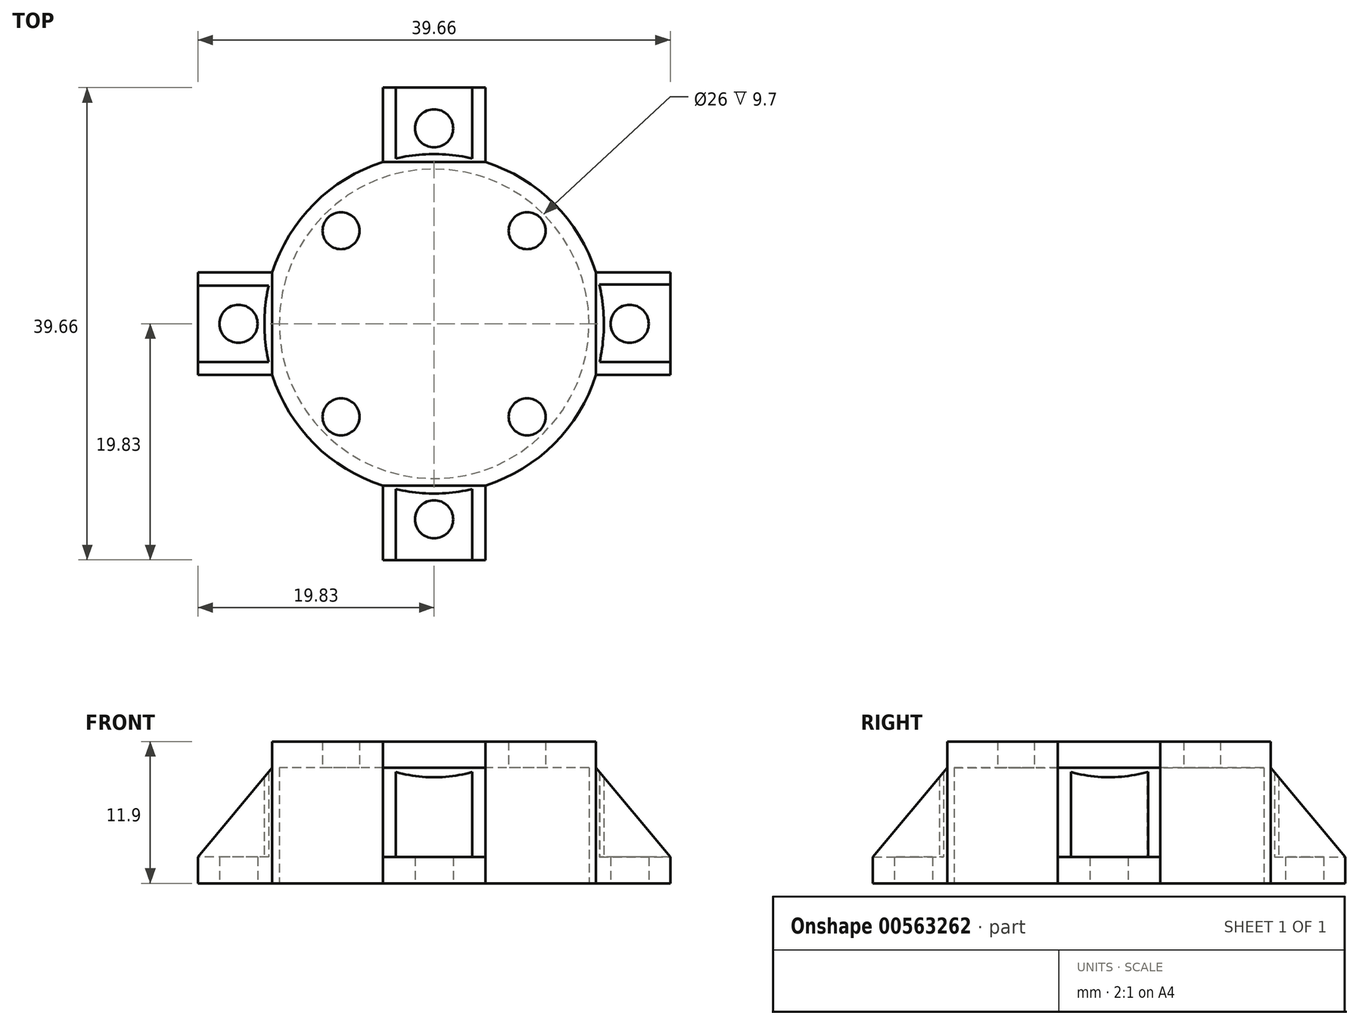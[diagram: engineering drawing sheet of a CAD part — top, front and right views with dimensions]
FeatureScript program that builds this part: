
annotation { "Feature Type Name" : "Feature", "Feature Type Description" : "" }
export const myFeature = defineFeature(function(context is Context, id is Id, definition is map)
    precondition{}
    {
        {
            var Q0;
            Q0=qCreatedBy(makeId("Top.planeOp"),FACE);
            var sketch = newSketch(context, id + "F0", { "sketchPlane" : qUnion([Q0])});
            skCircle(sketch, "E0", {"center": v(0, 0) * mm, "radius": 13 * mm});
            skLineSegment(sketch, "E1", {"start": v(0, 19.83) * mm, "end": v(4.3, 19.83) * mm});
            skLineSegment(sketch, "E2", {"start": v(4.3, 19.83) * mm, "end": v(4.3, 12.27) * mm});
            skLineSegment(sketch, "E3.MirrorCS", {"start": v(0, 19.83) * mm, "end": v(-4.3, 19.83) * mm});
            skLineSegment(sketch, "E4.MirrorCS", {"start": v(-4.3, 19.83) * mm, "end": v(-4.3, 12.27) * mm});
            skLineSegment(sketch, "E5", {"start": v(0, 0) * mm, "end": v(27.32, 0) * mm, "construction": true});
            skLineSegment(sketch, "E6", {"start": v(0, 0) * mm, "end": v(27.32, 27.32) * mm, "construction": true});
            skLineSegment(sketch, "E7", {"start": v(0, 19.83) * mm, "end": v(0, 13) * mm, "construction": true});
            skCircle(sketch, "E8", {"center": v(0, 16.42) * mm, "radius": 1.6 * mm});
            skLineSegment(sketch, "E9.MirrorCS", {"start": v(19.83, 0) * mm, "end": v(19.83, 4.3) * mm});
            skLineSegment(sketch, "E10.MirrorCS", {"start": v(19.83, 0) * mm, "end": v(19.83, -4.3) * mm});
            skLineSegment(sketch, "E11.MirrorCS", {"start": v(19.83, -4.3) * mm, "end": v(12.27, -4.3) * mm});
            skCircle(sketch, "E12.MirrorC", {"center": v(16.42, 0) * mm, "radius": 1.6 * mm});
            skLineSegment(sketch, "E13.MirrorCS", {"start": v(19.83, 4.3) * mm, "end": v(12.27, 4.3) * mm});
            skLineSegment(sketch, "E14.MirrorCS", {"start": v(0, -19.83) * mm, "end": v(4.3, -19.83) * mm});
            skLineSegment(sketch, "E15.MirrorCS", {"start": v(0, -19.83) * mm, "end": v(-4.3, -19.83) * mm});
            skLineSegment(sketch, "E16.MirrorCS", {"start": v(-4.3, -19.83) * mm, "end": v(-4.3, -12.27) * mm});
            skLineSegment(sketch, "E17.MirrorCS", {"start": v(4.3, -19.83) * mm, "end": v(4.3, -12.27) * mm});
            skCircle(sketch, "E18.MirrorC", {"center": v(0, -16.42) * mm, "radius": 1.6 * mm});
            skLineSegment(sketch, "E19", {"start": v(0, 0) * mm, "end": v(0, -28.1) * mm, "construction": true});
            skLineSegment(sketch, "E20.MirrorCS", {"start": v(-19.83, 4.3) * mm, "end": v(-12.27, 4.3) * mm});
            skLineSegment(sketch, "E21.MirrorCS", {"start": v(-19.83, 0) * mm, "end": v(-19.83, 4.3) * mm});
            skCircle(sketch, "E22.MirrorC", {"center": v(-16.42, 0) * mm, "radius": 1.6 * mm});
            skLineSegment(sketch, "E23.MirrorCS", {"start": v(-19.83, 0) * mm, "end": v(-19.83, -4.3) * mm});
            skLineSegment(sketch, "E24.MirrorCS", {"start": v(-19.83, -4.3) * mm, "end": v(-12.27, -4.3) * mm});
            skCircle(sketch, "E25", {"center": v(0, 0) * mm, "radius": 14.25 * mm});
            skSolve(sketch);
        }
        {
            var Q0;
            {var subQ5=sQuery(id+"F0.wireOp",EDGE,"E1");Q0=makeQuery(id+"F0.imprint","IMPRINT",FACE,{"disambiguationData":[TD([[makeQuery(id+"F0.imprint","IMPRINT",EDGE,{"derivedFrom":subQ5}),-1.0]])]});}
            var Q1;
            {var subQ0=sQuery(id+"F0.wireOp",EDGE,"E4.MirrorCS");var subQ1=sQuery(id+"F0.wireOp",EDGE,"E0");var subQ2=makeQuery(id+"F0.imprint","INTERSECT",VERTEX,{"derivedFrom":[subQ1,subQ0]});Q1=makeQuery(id+"F0.imprint","IMPRINT",FACE,{"disambiguationData":[TD([[makeQuery(id+"F0.imprint","IMPRINT",EDGE,{"disambiguationData":[TD([[subQ2,-1.0]])],"derivedFrom":subQ1}),-1.0]])]});}
            var Q2;
            {var subQ0=sQuery(id+"F0.wireOp",EDGE,"E2");var subQ1=sQuery(id+"F0.wireOp",EDGE,"E0");var subQ2=makeQuery(id+"F0.imprint","INTERSECT",VERTEX,{"derivedFrom":[subQ1,subQ0]});Q2=makeQuery(id+"F0.imprint","IMPRINT",FACE,{"disambiguationData":[TD([[makeQuery(id+"F0.imprint","IMPRINT",EDGE,{"disambiguationData":[TD([[subQ2,-1.0]])],"derivedFrom":subQ1}),-1.0]])]});}
            var Q3;
            {var subQ0=sQuery(id+"F0.wireOp",EDGE,"E2");var subQ1=sQuery(id+"F0.wireOp",EDGE,"E0");var subQ2=makeQuery(id+"F0.imprint","INTERSECT",VERTEX,{"derivedFrom":[subQ1,subQ0]});Q3=makeQuery(id+"F0.imprint","IMPRINT",FACE,{"disambiguationData":[TD([[makeQuery(id+"F0.imprint","IMPRINT",EDGE,{"disambiguationData":[TD([[subQ2,1.0]])],"derivedFrom":subQ1}),-1.0]])]});}
            var Q4;
            {var subQ0=sQuery(id+"F0.wireOp",EDGE,"E11.MirrorCS");var subQ1=sQuery(id+"F0.wireOp",EDGE,"E0");var subQ2=makeQuery(id+"F0.imprint","INTERSECT",VERTEX,{"derivedFrom":[subQ1,subQ0]});Q4=makeQuery(id+"F0.imprint","IMPRINT",FACE,{"disambiguationData":[TD([[makeQuery(id+"F0.imprint","IMPRINT",EDGE,{"disambiguationData":[TD([[subQ2,-1.0]])],"derivedFrom":subQ1}),-1.0]])]});}
            var Q5;
            {var subQ4=sQuery(id+"F0.wireOp",EDGE,"E9.MirrorCS");Q5=makeQuery(id+"F0.imprint","IMPRINT",FACE,{"disambiguationData":[TD([[makeQuery(id+"F0.imprint","IMPRINT",EDGE,{"derivedFrom":subQ4}),1.0]])]});}
            var Q6;
            {var subQ0=sQuery(id+"F0.wireOp",EDGE,"E11.MirrorCS");var subQ1=sQuery(id+"F0.wireOp",EDGE,"E0");var subQ2=makeQuery(id+"F0.imprint","INTERSECT",VERTEX,{"derivedFrom":[subQ1,subQ0]});Q6=makeQuery(id+"F0.imprint","IMPRINT",FACE,{"disambiguationData":[TD([[makeQuery(id+"F0.imprint","IMPRINT",EDGE,{"disambiguationData":[TD([[subQ2,1.0]])],"derivedFrom":subQ1}),-1.0]])]});}
            var Q7;
            {var subQ0=sQuery(id+"F0.wireOp",EDGE,"E16.MirrorCS");var subQ1=sQuery(id+"F0.wireOp",EDGE,"E0");var subQ2=makeQuery(id+"F0.imprint","INTERSECT",VERTEX,{"derivedFrom":[subQ1,subQ0]});Q7=makeQuery(id+"F0.imprint","IMPRINT",FACE,{"disambiguationData":[TD([[makeQuery(id+"F0.imprint","IMPRINT",EDGE,{"disambiguationData":[TD([[subQ2,-1.0]])],"derivedFrom":subQ1}),-1.0]])]});}
            var Q8;
            {var subQ0=sQuery(id+"F0.wireOp",EDGE,"E16.MirrorCS");var subQ1=sQuery(id+"F0.wireOp",EDGE,"E0");var subQ2=makeQuery(id+"F0.imprint","INTERSECT",VERTEX,{"derivedFrom":[subQ1,subQ0]});Q8=makeQuery(id+"F0.imprint","IMPRINT",FACE,{"disambiguationData":[TD([[makeQuery(id+"F0.imprint","IMPRINT",EDGE,{"disambiguationData":[TD([[subQ2,1.0]])],"derivedFrom":subQ1}),-1.0]])]});}
            var Q9;
            {var subQ0=sQuery(id+"F0.wireOp",EDGE,"E20.MirrorCS");var subQ1=sQuery(id+"F0.wireOp",EDGE,"E0");var subQ2=makeQuery(id+"F0.imprint","INTERSECT",VERTEX,{"derivedFrom":[subQ1,subQ0]});Q9=makeQuery(id+"F0.imprint","IMPRINT",FACE,{"disambiguationData":[TD([[makeQuery(id+"F0.imprint","IMPRINT",EDGE,{"disambiguationData":[TD([[subQ2,-1.0]])],"derivedFrom":subQ1}),-1.0]])]});}
            var Q10;
            {var subQ1=sQuery(id+"F0.wireOp",EDGE,"E21.MirrorCS");Q10=makeQuery(id+"F0.imprint","IMPRINT",FACE,{"disambiguationData":[TD([[makeQuery(id+"F0.imprint","IMPRINT",EDGE,{"derivedFrom":subQ1}),-1.0]])]});}
            var Q11;
            {var subQ1=sQuery(id+"F0.wireOp",EDGE,"E14.MirrorCS");Q11=makeQuery(id+"F0.imprint","IMPRINT",FACE,{"disambiguationData":[TD([[makeQuery(id+"F0.imprint","IMPRINT",EDGE,{"derivedFrom":subQ1}),1.0]])]});}
            extrude(context, id + "F1", {"entities" : qUnion([Q0, Q1, Q2, Q3, Q4, Q5, Q6, Q7, Q8, Q9, Q10, Q11]), "depth" : 2.2 * mm, "offsetDistance" : 25 * mm});
        }
        {
            var Q0;
            Q0=makeQuery(id+"F1.opExtrude","CAP_FACE",FACE,{"disambiguationData":[OSD([sQuery(id+"F0.wireOp",EDGE,"E0"),sQuery(id+"F0.wireOp",EDGE,"E1"),sQuery(id+"F0.wireOp",EDGE,"E2"),sQuery(id+"F0.wireOp",EDGE,"E3.MirrorCS"),sQuery(id+"F0.wireOp",EDGE,"E4.MirrorCS"),sQuery(id+"F0.wireOp",EDGE,"E8"),sQuery(id+"F0.wireOp",EDGE,"E9.MirrorCS"),sQuery(id+"F0.wireOp",EDGE,"E10.MirrorCS"),sQuery(id+"F0.wireOp",EDGE,"E11.MirrorCS"),sQuery(id+"F0.wireOp",EDGE,"E12.MirrorC"),sQuery(id+"F0.wireOp",EDGE,"E13.MirrorCS"),sQuery(id+"F0.wireOp",EDGE,"E14.MirrorCS"),sQuery(id+"F0.wireOp",EDGE,"E15.MirrorCS"),sQuery(id+"F0.wireOp",EDGE,"E16.MirrorCS"),sQuery(id+"F0.wireOp",EDGE,"E17.MirrorCS"),sQuery(id+"F0.wireOp",EDGE,"E18.MirrorC"),sQuery(id+"F0.wireOp",EDGE,"E20.MirrorCS"),sQuery(id+"F0.wireOp",EDGE,"E21.MirrorCS"),sQuery(id+"F0.wireOp",EDGE,"E22.MirrorC"),sQuery(id+"F0.wireOp",EDGE,"E23.MirrorCS"),sQuery(id+"F0.wireOp",EDGE,"E24.MirrorCS"),sQuery(id+"F0.wireOp",EDGE,"E25")])],"isStart":false});
            var sketch = newSketch(context, id + "F2", { "sketchPlane" : qUnion([Q0])});
            skCircle(sketch, "E26", {"center": v(0, 0) * mm, "radius": 14.25 * mm});
            skPoint(sketch, "E26.first.point", {"position": v(-13.59, 4.3) * mm});
            skPoint(sketch, "E26.second.point", {"position": v(4.3, 13.59) * mm});
            skPoint(sketch, "E26.third.point", {"position": v(4.3, -13.59) * mm});
            skLineSegment(sketch, "E27", {"start": v(-4.3, 13.59) * mm, "end": v(-4.3, 19.83) * mm});
            skLineSegment(sketch, "E28", {"start": v(-4.3, 19.83) * mm, "end": v(4.3, 19.83) * mm});
            skLineSegment(sketch, "E29", {"start": v(4.3, 19.83) * mm, "end": v(4.3, 13.59) * mm});
            skLineSegment(sketch, "E30", {"start": v(13.59, 4.3) * mm, "end": v(19.83, 4.3) * mm});
            skLineSegment(sketch, "E31", {"start": v(19.83, 4.3) * mm, "end": v(19.83, -4.3) * mm});
            skLineSegment(sketch, "E32", {"start": v(19.83, -4.3) * mm, "end": v(13.59, -4.3) * mm});
            skLineSegment(sketch, "E33", {"start": v(4.3, -19.83) * mm, "end": v(-4.3, -19.83) * mm});
            skLineSegment(sketch, "E34", {"start": v(-4.3, -19.83) * mm, "end": v(-4.3, -13.59) * mm});
            skLineSegment(sketch, "E35", {"start": v(-13.59, -4.3) * mm, "end": v(-19.83, -4.3) * mm});
            skLineSegment(sketch, "E36", {"start": v(-19.83, -4.3) * mm, "end": v(-19.83, 4.3) * mm});
            skLineSegment(sketch, "E37", {"start": v(-19.83, 4.3) * mm, "end": v(-13.59, 4.3) * mm});
            skLineSegment(sketch, "E38.0", {"start": v(-3.2, 13.59) * mm, "end": v(-3.2, 19.83) * mm});
            skLineSegment(sketch, "E39.0", {"start": v(3.2, 19.83) * mm, "end": v(3.2, 13.59) * mm});
            skLineSegment(sketch, "E40.0", {"start": v(13.59, 3.3) * mm, "end": v(19.83, 3.3) * mm});
            skLineSegment(sketch, "E41.0", {"start": v(19.83, -3.2) * mm, "end": v(13.59, -3.2) * mm});
            skLineSegment(sketch, "E42.0", {"start": v(3.2, -19.83) * mm, "end": v(3.2, -13.59) * mm});
            skLineSegment(sketch, "E43.0", {"start": v(-3.2, -19.83) * mm, "end": v(-3.2, -13.59) * mm});
            skLineSegment(sketch, "E44.0", {"start": v(-19.83, 3.2) * mm, "end": v(-13.59, 3.2) * mm});
            skLineSegment(sketch, "E45.0", {"start": v(-13.59, -3.2) * mm, "end": v(-19.83, -3.2) * mm});
            skSolve(sketch);
        }
        {
            var Q0;
            {var subQ0=sQuery(id+"F2.wireOp",EDGE,"E29");Q0=makeQuery(id+"F2.imprint","IMPRINT",FACE,{"disambiguationData":[TD([[makeQuery(id+"F2.imprint","IMPRINT",EDGE,{"derivedFrom":subQ0}),-1.0]])]});}
            var Q1;
            Q1=makeQuery(id+"F2.imprint","IMPRINT",FACE,{"disambiguationData":[TD([[makeQuery(id+"F2.imprint","IMPRINT",EDGE,{"derivedFrom":makeQuery(id+"F1.opExtrude","CAP_EDGE",EDGE,{"disambiguationData":[OSD([sQuery(id+"F0.wireOp",EDGE,"E0")])],"isStart":false})}),-1.0]])]});
            var Q2;
            {var subQ0=sQuery(id+"F2.wireOp",EDGE,"E27");Q2=makeQuery(id+"F2.imprint","IMPRINT",FACE,{"disambiguationData":[TD([[makeQuery(id+"F2.imprint","IMPRINT",EDGE,{"derivedFrom":subQ0}),1.0]])]});}
            var Q3;
            {var subQ0=sQuery(id+"F2.wireOp",EDGE,"E30");Q3=makeQuery(id+"F2.imprint","IMPRINT",FACE,{"disambiguationData":[TD([[makeQuery(id+"F2.imprint","IMPRINT",EDGE,{"derivedFrom":subQ0}),1.0]])]});}
            var Q4;
            {var subQ0=sQuery(id+"F2.wireOp",EDGE,"E32");Q4=makeQuery(id+"F2.imprint","IMPRINT",FACE,{"disambiguationData":[TD([[makeQuery(id+"F2.imprint","IMPRINT",EDGE,{"derivedFrom":subQ0}),-1.0]])]});}
            var Q5;
            {var subQ0=sQuery(id+"F2.wireOp",EDGE,"E37");Q5=makeQuery(id+"F2.imprint","IMPRINT",FACE,{"disambiguationData":[TD([[makeQuery(id+"F2.imprint","IMPRINT",EDGE,{"derivedFrom":subQ0}),-1.0]])]});}
            var Q6;
            {var subQ0=sQuery(id+"F2.wireOp",EDGE,"E35");Q6=makeQuery(id+"F2.imprint","IMPRINT",FACE,{"disambiguationData":[TD([[makeQuery(id+"F2.imprint","IMPRINT",EDGE,{"derivedFrom":subQ0}),1.0]])]});}
            var Q7;
            {var subQ0=sQuery(id+"F2.wireOp",EDGE,"E34");Q7=makeQuery(id+"F2.imprint","IMPRINT",FACE,{"disambiguationData":[TD([[makeQuery(id+"F2.imprint","IMPRINT",EDGE,{"derivedFrom":subQ0}),-1.0]])]});}
            var Q8;
            {var subQ1=makeQuery(id+"F1.opExtrude","CAP_EDGE",EDGE,{"disambiguationData":[OSD([sQuery(id+"F0.wireOp",EDGE,"E17.MirrorCS")])],"isStart":false});Q8=makeQuery(id+"F2.imprint","IMPRINT",FACE,{"disambiguationData":[TD([[makeQuery(id+"F2.imprint","IMPRINT",EDGE,{"derivedFrom":subQ1}),1.0]])]});}
            extrude(context, id + "F3", {"entities" : qUnion([Q0, Q1, Q2, Q3, Q4, Q5, Q6, Q7, Q8]), "operationType" : NewBodyOperationType.ADD, "depth" : 7.5 * mm, "offsetDistance" : 25 * mm});
        }
        {
            var Q0;
            Q0=makeQuery(id+"F3.boolean.opBoolean","MERGE",FACE,{"derivedFrom":[makeQuery(id+"F1.opExtrude","SWEPT_FACE",FACE,{"disambiguationData":[OSD([sQuery(id+"F0.wireOp",EDGE,"E24.MirrorCS")])]}),makeQuery(id+"F3.opExtrude","SWEPT_FACE",FACE,{"disambiguationData":[OSD([sQuery(id+"F2.wireOp",EDGE,"E35")])]})]});
            var sketch = newSketch(context, id + "F4", { "sketchPlane" : qUnion([Q0])});
            skLineSegment(sketch, "E46", {"start": v(-19.83, 0) * mm, "end": v(-19.83, 2.2) * mm, "construction": true});
            skLineSegment(sketch, "E47", {"start": v(-19.83, 2.2) * mm, "end": v(-13.59, 9.7) * mm});
            skLineSegment(sketch, "E48", {"start": v(-19.83, 2.2) * mm, "end": v(-13.59, 2.2) * mm});
            skLineSegment(sketch, "E49", {"start": v(-13.59, 2.2) * mm, "end": v(-13.59, 9.7) * mm});
            skSolve(sketch);
        }
        {
            var Q0;
            {var subQ0=sQuery(id+"F4.wireOp",EDGE,"E47");Q0=makeQuery(id+"F4.imprint","IMPRINT",FACE,{"disambiguationData":[TD([[makeQuery(id+"F4.imprint","IMPRINT",EDGE,{"derivedFrom":subQ0}),1.0]])]});}
            extrude(context, id + "F5", {"entities" : qUnion([Q0]), "operationType" : NewBodyOperationType.REMOVE, "endBound" : BoundingType.THROUGH_ALL, "oppositeDirection" : true, "depth" : 25 * mm, "offsetDistance" : 25 * mm});
        }
        {
            var Q0;
            Q0=makeQuery(id+"F3.boolean.opBoolean","MERGE",FACE,{"derivedFrom":[makeQuery(id+"F1.opExtrude","SWEPT_FACE",FACE,{"disambiguationData":[OSD([sQuery(id+"F0.wireOp",EDGE,"E11.MirrorCS")])]}),makeQuery(id+"F3.opExtrude","SWEPT_FACE",FACE,{"disambiguationData":[OSD([sQuery(id+"F2.wireOp",EDGE,"E32")])]})]});
            var sketch = newSketch(context, id + "F6", { "sketchPlane" : qUnion([Q0])});
            skLineSegment(sketch, "E50", {"start": v(13.59, 0) * mm, "end": v(13.59, 2.2) * mm, "construction": true});
            skLineSegment(sketch, "E51", {"start": v(13.59, 2.2) * mm, "end": v(19.83, 2.2) * mm});
            skLineSegment(sketch, "E52", {"start": v(19.83, 2.2) * mm, "end": v(13.59, 9.7) * mm});
            skLineSegment(sketch, "E53", {"start": v(13.59, 9.7) * mm, "end": v(13.59, 2.2) * mm});
            skSolve(sketch);
        }
        {
            var Q0;
            {var subQ0=sQuery(id+"F6.wireOp",EDGE,"E52");Q0=makeQuery(id+"F6.imprint","IMPRINT",FACE,{"disambiguationData":[TD([[makeQuery(id+"F6.imprint","IMPRINT",EDGE,{"derivedFrom":subQ0}),-1.0]])]});}
            extrude(context, id + "F7", {"entities" : qUnion([Q0]), "operationType" : NewBodyOperationType.REMOVE, "endBound" : BoundingType.THROUGH_ALL, "oppositeDirection" : true, "depth" : 25 * mm, "offsetDistance" : 25 * mm});
        }
        {
            var Q0;
            Q0=makeQuery(id+"F3.boolean.opBoolean","MERGE",FACE,{"derivedFrom":[makeQuery(id+"F1.opExtrude","SWEPT_FACE",FACE,{"disambiguationData":[OSD([sQuery(id+"F0.wireOp",EDGE,"E16.MirrorCS")])]}),makeQuery(id+"F3.opExtrude","SWEPT_FACE",FACE,{"disambiguationData":[OSD([sQuery(id+"F2.wireOp",EDGE,"E34")])]})]});
            var sketch = newSketch(context, id + "F8", { "sketchPlane" : qUnion([Q0])});
            skLineSegment(sketch, "E54", {"start": v(13.59, 0) * mm, "end": v(13.59, 2.2) * mm, "construction": true});
            skLineSegment(sketch, "E55", {"start": v(13.59, 2.2) * mm, "end": v(19.83, 2.2) * mm});
            skLineSegment(sketch, "E56", {"start": v(19.83, 2.2) * mm, "end": v(13.59, 9.7) * mm});
            skLineSegment(sketch, "E57", {"start": v(13.59, 9.7) * mm, "end": v(13.59, 2.2) * mm});
            skSolve(sketch);
        }
        {
            var Q0;
            {var subQ0=sQuery(id+"F8.wireOp",EDGE,"E56");Q0=makeQuery(id+"F8.imprint","IMPRINT",FACE,{"disambiguationData":[TD([[makeQuery(id+"F8.imprint","IMPRINT",EDGE,{"derivedFrom":subQ0}),-1.0]])]});}
            extrude(context, id + "F9", {"entities" : qUnion([Q0]), "operationType" : NewBodyOperationType.REMOVE, "endBound" : BoundingType.THROUGH_ALL, "oppositeDirection" : true, "depth" : 25 * mm, "offsetDistance" : 25 * mm});
        }
        {
            var Q0;
            Q0=makeQuery(id+"F3.boolean.opBoolean","MERGE",FACE,{"derivedFrom":[makeQuery(id+"F1.opExtrude","SWEPT_FACE",FACE,{"disambiguationData":[OSD([sQuery(id+"F0.wireOp",EDGE,"E4.MirrorCS")])]}),makeQuery(id+"F3.opExtrude","SWEPT_FACE",FACE,{"disambiguationData":[OSD([sQuery(id+"F2.wireOp",EDGE,"E27")])]})]});
            var sketch = newSketch(context, id + "F10", { "sketchPlane" : qUnion([Q0])});
            skLineSegment(sketch, "E58", {"start": v(-13.59, 0) * mm, "end": v(-13.59, 2.2) * mm, "construction": true});
            skLineSegment(sketch, "E59", {"start": v(-13.59, 2.2) * mm, "end": v(-19.83, 2.2) * mm});
            skLineSegment(sketch, "E60", {"start": v(-19.83, 2.2) * mm, "end": v(-13.59, 9.7) * mm});
            skLineSegment(sketch, "E61", {"start": v(-13.59, 9.7) * mm, "end": v(-13.59, 2.2) * mm});
            skSolve(sketch);
        }
        {
            var Q0;
            {var subQ0=sQuery(id+"F10.wireOp",EDGE,"E60");Q0=makeQuery(id+"F10.imprint","IMPRINT",FACE,{"disambiguationData":[TD([[makeQuery(id+"F10.imprint","IMPRINT",EDGE,{"derivedFrom":subQ0}),1.0]])]});}
            extrude(context, id + "F11", {"entities" : qUnion([Q0]), "operationType" : NewBodyOperationType.REMOVE, "endBound" : BoundingType.THROUGH_ALL, "oppositeDirection" : true, "depth" : 25 * mm, "offsetDistance" : 25 * mm});
        }
        {
            var Q0;
            Q0=makeQuery(id+"F3.opExtrude","CAP_FACE",FACE,{"disambiguationData":[OSD([sQuery(id+"F0.wireOp",EDGE,"E0"),sQuery(id+"F0.wireOp",EDGE,"E17.MirrorCS"),sQuery(id+"F2.wireOp",EDGE,"E26"),sQuery(id+"F2.wireOp",EDGE,"E27"),sQuery(id+"F2.wireOp",EDGE,"E28"),sQuery(id+"F2.wireOp",EDGE,"E29"),sQuery(id+"F2.wireOp",EDGE,"E30"),sQuery(id+"F2.wireOp",EDGE,"E31"),sQuery(id+"F2.wireOp",EDGE,"E32"),sQuery(id+"F2.wireOp",EDGE,"E33"),sQuery(id+"F2.wireOp",EDGE,"E34"),sQuery(id+"F2.wireOp",EDGE,"E35"),sQuery(id+"F2.wireOp",EDGE,"E36"),sQuery(id+"F2.wireOp",EDGE,"E37"),sQuery(id+"F2.wireOp",EDGE,"E38.0"),sQuery(id+"F2.wireOp",EDGE,"E39.0"),sQuery(id+"F2.wireOp",EDGE,"E40.0"),sQuery(id+"F2.wireOp",EDGE,"E41.0"),sQuery(id+"F2.wireOp",EDGE,"E42.0"),sQuery(id+"F2.wireOp",EDGE,"E43.0"),sQuery(id+"F2.wireOp",EDGE,"E44.0"),sQuery(id+"F2.wireOp",EDGE,"E45.0")])],"isStart":false});
            var sketch = newSketch(context, id + "F12", { "sketchPlane" : qUnion([Q0])});
            skCircle(sketch, "E62", {"center": v(0, 0) * mm, "radius": 14.25 * mm});
            skPoint(sketch, "E62.first.point", {"position": v(-13.59, 4.3) * mm});
            skPoint(sketch, "E62.second.point", {"position": v(4.3, 13.59) * mm});
            skPoint(sketch, "E62.third.point", {"position": v(13.59, -4.3) * mm});
            skLineSegment(sketch, "E63", {"start": v(0, 0) * mm, "end": v(29.59, 0) * mm, "construction": true});
            skLineSegment(sketch, "E64", {"start": v(29.59, 29.59) * mm, "end": v(0, 0) * mm, "construction": true});
            skLineSegment(sketch, "E65", {"start": v(0, 0) * mm, "end": v(0, 30.25) * mm, "construction": true});
            skCircle(sketch, "E66", {"center": v(0, 0) * mm, "radius": 11.05 * mm, "construction": true});
            skCircle(sketch, "E67", {"center": v(7.81, 7.81) * mm, "radius": 1.55 * mm});
            skCircle(sketch, "E68.MirrorC", {"center": v(-7.81, 7.81) * mm, "radius": 1.55 * mm});
            skCircle(sketch, "E69.MirrorC", {"center": v(7.81, -7.81) * mm, "radius": 1.55 * mm});
            skCircle(sketch, "E70.MirrorC", {"center": v(-7.81, -7.81) * mm, "radius": 1.55 * mm});
            skSolve(sketch);
        }
        {
            var Q0;
            Q0=makeQuery(id+"F12.imprint","IMPRINT",FACE,{"disambiguationData":[TD([[makeQuery(id+"F12.imprint","IMPRINT",EDGE,{"derivedFrom":sQuery(id+"F12.wireOp",EDGE,"E67")}),-1.0]])]});
            var Q1;
            Q1=makeQuery(id+"F12.imprint","IMPRINT",FACE,{"disambiguationData":[TD([[makeQuery(id+"F12.imprint","IMPRINT",EDGE,{"derivedFrom":makeQuery(id+"F3.opExtrude","CAP_EDGE",EDGE,{"disambiguationData":[OSD([sQuery(id+"F0.wireOp",EDGE,"E0")])],"isStart":false})}),-1.0]])]});
            extrude(context, id + "F13", {"entities" : qUnion([Q0, Q1]), "operationType" : NewBodyOperationType.ADD, "depth" : 2.2 * mm, "offsetDistance" : 25 * mm});
        }
    });
